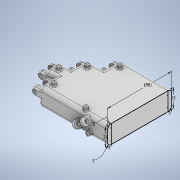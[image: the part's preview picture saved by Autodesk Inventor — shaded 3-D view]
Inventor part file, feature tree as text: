
AUTODESK INVENTOR PART (.ipt)
format: ipt  version: 2022 (Build 260153000, 153)  size: 1,100,288 bytes
history: native  units: mm
features: sketch x27, extrude x26, fillet x8, other x6
ambient origin geometry x8: Origin, YZ Plane, XZ Plane, XY Plane, X Axis, Y Axis, Z Axis, Center Point
bodies: Solide1 (feature_tree)
feature tree (67):
  extrude  "Extrusion1"  Depth=110.0mm
  other  "Plan de construction3"
  extrude  "Extrusion9"  Depth=88.0mm
  extrude  "Extrusion10"  Depth=25.0mm TaperAngle=0.0deg
  extrude  "Extrusion11"  Depth=25.0mm
  extrude  "Extrusion13"  Depth=22.0mm
  extrude  "Extrusion14"  Depth=22.0mm
  sketch  "Esquisse30"
  sketch  "Esquisse31"
  sketch  "Esquisse32"
  sketch  "Esquisse33"
  extrude  "Extrusion25"  Depth=22.0mm
  extrude  "Extrusion26"  Depth=22.0mm
  extrude  "Extrusion27"  Depth=2.0mm
  extrude  "Extrusion28"  Depth=2.0mm
  sketch  "Esquisse34"
  sketch  "Esquisse35"
  sketch  "Esquisse36"
  sketch  "Esquisse37"
  extrude  "Extrusion29"  Depth=2.0mm
  extrude  "Extrusion30"  Depth=20.0mm
  extrude  "Extrusion31"  Depth=6.0mm
  extrude  "Extrusion32"  Depth=8.0mm
  extrude  "Extrusion33"  Depth=5.0mm
  extrude  "Extrusion34"  Depth=5.0mm
  extrude  "Extrusion35"  Depth=10.0mm TaperAngle=0.0deg
  extrude  "Extrusion36"  Depth=5.0mm
  extrude  "Extrusion37"  Depth=20.0mm TaperAngle=0.0deg
  extrude  "Extrusion38"  Depth=15.0mm TaperAngle=0.0deg
  extrude  "Extrusion39"  Depth=17.0mm TaperAngle=0.0deg
  extrude  "Extrusion40"  Depth=40.0mm TaperAngle=0.0deg
  other  "Révolution1"
  fillet  "Congé14"  Radius=20.0mm
  fillet  "Congé15"  Radius=6.0mm
  fillet  "Congé16"  Radius=7.0mm
  fillet  "Congé17"  Radius=5.0mm
  fillet  "Congé18"  Radius=6.0mm
  fillet  "Congé20"  Radius=10.0mm
  fillet  "Congé21"  Radius=20.0mm
  extrude  "Extrusion41"  Depth=5.0mm
  other  "Révolution3"
  extrude  "Extrusion42"  Depth=10.0mm
  extrude  "Extrusion43"  Depth=5.0mm
  extrude  "Extrusion44"  Depth=5.0mm
  other  "Révolution4"
  other  "Révolution5"
  other  "Révolution6"
  fillet  "Congé22"  Radius=10.0mm
  sketch  "Esquisse57"
  sketch  "Esquisse18"
  sketch  "Esquisse38"
  sketch  "Esquisse40"
  sketch  "Esquisse41"
  sketch  "Esquisse42"
  sketch  "Esquisse43"
  sketch  "Esquisse44"
  sketch  "Esquisse45"
  sketch  "Esquisse46"
  sketch  "Esquisse47"
  sketch  "Esquisse48"
  sketch  "Esquisse50"
  sketch  "Esquisse51"
  sketch  "Esquisse52"
  sketch  "Esquisse53"
  sketch  "Esquisse54"
  sketch  "Esquisse55"
  sketch  "Esquisse56"
